annotation { "Feature Type Name" : "Feature", "Feature Type Description" : "" }
export const myFeature = defineFeature(function(context is Context, id is Id, definition is map)
    precondition{}
    {
        {
            var Q0;
            Q0=qCreatedBy(makeId("Front.planeOp"),FACE);
            var sketch = newSketch(context, id + "F0", { "sketchPlane" : qUnion([Q0])});
            skLineSegment(sketch, "E0.bottom", {"start": v(11430, -29718) * mm, "end": v(-11430, -29718) * mm});
            skLineSegment(sketch, "E0.top", {"start": v(11430, 29718) * mm, "end": v(-11430, 29718) * mm});
            skLineSegment(sketch, "E0.left", {"start": v(11430, -29718) * mm, "end": v(11430, 29718) * mm});
            skLineSegment(sketch, "E0.right", {"start": v(-11430, -29718) * mm, "end": v(-11430, 29718) * mm});
            skPoint(sketch, "E0.middle", {"position": v(0, 0) * mm});
            skPoint(sketch, "E1.endSnap0", {"position": v(0, -29718) * mm});
            skLineSegment(sketch, "E2", {"start": v(0, 0) * mm, "end": v(0, 32682.02) * mm, "construction": true});
            skLineSegment(sketch, "E3.bottom", {"start": v(-11430, -29718) * mm, "end": v(-3810, -29718) * mm});
            skLineSegment(sketch, "E3.left", {"start": v(-11430, -29718) * mm, "end": v(-11430, -22098) * mm});
            skLineSegment(sketch, "E4", {"start": v(-11430, -22098) * mm, "end": v(-3810, -22098) * mm});
            skLineSegment(sketch, "E5", {"start": v(-3810, -22098) * mm, "end": v(-3810, -29718) * mm});
            skLineSegment(sketch, "E6.bottom", {"start": v(-3810, -22098) * mm, "end": v(3810, -22098) * mm});
            skLineSegment(sketch, "E6.top", {"start": v(-3810, -29718) * mm, "end": v(3810, -29718) * mm});
            skLineSegment(sketch, "E6.right", {"start": v(3810, -22098) * mm, "end": v(3810, -29718) * mm});
            skLineSegment(sketch, "E7.bottom", {"start": v(3810, -22098) * mm, "end": v(11430, -22098) * mm});
            skLineSegment(sketch, "E7.top", {"start": v(3810, -29718) * mm, "end": v(11430, -29718) * mm});
            skLineSegment(sketch, "E7.right", {"start": v(11430, -22098) * mm, "end": v(11430, -29718) * mm});
            skLineSegment(sketch, "E8.top", {"start": v(-11430, -14478) * mm, "end": v(-3810, -14478) * mm});
            skLineSegment(sketch, "E8.left", {"start": v(-11430, -22098) * mm, "end": v(-11430, -14478) * mm});
            skLineSegment(sketch, "E8.right", {"start": v(-3810, -22098) * mm, "end": v(-3810, -14478) * mm});
            skLineSegment(sketch, "E9.top", {"start": v(-11430, -6858) * mm, "end": v(-3810, -6858) * mm});
            skLineSegment(sketch, "E9.left", {"start": v(-11430, -14478) * mm, "end": v(-11430, -6858) * mm});
            skLineSegment(sketch, "E9.right", {"start": v(-3810, -14478) * mm, "end": v(-3810, -6858) * mm});
            skLineSegment(sketch, "E10.top", {"start": v(-11430, 0) * mm, "end": v(-3810, 0) * mm});
            skLineSegment(sketch, "E10.left", {"start": v(-11430, -6858) * mm, "end": v(-11430, 0) * mm});
            skLineSegment(sketch, "E10.right", {"start": v(-3810, -6858) * mm, "end": v(-3810, 0) * mm});
            skLineSegment(sketch, "E11.top", {"start": v(-11430, 7202.75) * mm, "end": v(-3810, 7202.75) * mm});
            skLineSegment(sketch, "E11.left", {"start": v(-11430, 0) * mm, "end": v(-11430, 7202.75) * mm});
            skLineSegment(sketch, "E11.right", {"start": v(-3810, 0) * mm, "end": v(-3810, 7202.75) * mm});
            skLineSegment(sketch, "E12.top", {"start": v(-3810, -14478) * mm, "end": v(3810, -14478) * mm});
            skLineSegment(sketch, "E12.right", {"start": v(3810, -22098) * mm, "end": v(3810, -14478) * mm});
            skLineSegment(sketch, "E13.top", {"start": v(3810, -14478) * mm, "end": v(11430, -14478) * mm});
            skLineSegment(sketch, "E13.right", {"start": v(11430, -22098) * mm, "end": v(11430, -14478) * mm});
            skLineSegment(sketch, "E14.bottom", {"start": v(11430, -14478) * mm, "end": v(3810, -14478) * mm});
            skLineSegment(sketch, "E14.top", {"start": v(11430, -6858) * mm, "end": v(3810, -6858) * mm});
            skLineSegment(sketch, "E14.left", {"start": v(11430, -14478) * mm, "end": v(11430, -6858) * mm});
            skLineSegment(sketch, "E14.right", {"start": v(3810, -14478) * mm, "end": v(3810, -6858) * mm});
            skLineSegment(sketch, "E15.bottom", {"start": v(3810, -14478) * mm, "end": v(-3810, -14478) * mm});
            skLineSegment(sketch, "E15.top", {"start": v(3810, -6858) * mm, "end": v(-3810, -6858) * mm});
            skLineSegment(sketch, "E16.bottom", {"start": v(-3810, -6858) * mm, "end": v(3810, -6858) * mm});
            skLineSegment(sketch, "E16.top", {"start": v(-3810, 0) * mm, "end": v(3810, 0) * mm});
            skLineSegment(sketch, "E16.right", {"start": v(3810, -6858) * mm, "end": v(3810, 0) * mm});
            skLineSegment(sketch, "E17.bottom", {"start": v(3810, 0) * mm, "end": v(11430, 0) * mm});
            skLineSegment(sketch, "E17.top", {"start": v(3810, -6858) * mm, "end": v(11430, -6858) * mm});
            skLineSegment(sketch, "E17.left", {"start": v(3810, 0) * mm, "end": v(3810, -6858) * mm});
            skLineSegment(sketch, "E17.right", {"start": v(11430, 0) * mm, "end": v(11430, -6858) * mm});
            skLineSegment(sketch, "E18.bottom", {"start": v(11430, 0) * mm, "end": v(3810, 0) * mm});
            skLineSegment(sketch, "E18.top", {"start": v(11430, 7202.75) * mm, "end": v(3810, 7202.75) * mm});
            skLineSegment(sketch, "E18.left", {"start": v(11430, 0) * mm, "end": v(11430, 7202.75) * mm});
            skLineSegment(sketch, "E18.right", {"start": v(3810, 0) * mm, "end": v(3810, 7202.75) * mm});
            skLineSegment(sketch, "E19.bottom", {"start": v(3810, 0) * mm, "end": v(-3810, 0) * mm});
            skLineSegment(sketch, "E19.top", {"start": v(3810, 7202.75) * mm, "end": v(-3810, 7202.75) * mm});
            skSolve(sketch);
        }
        {
            var Q0;
            Q0=qCreatedBy(makeId("Front.planeOp"),FACE);
            var sketch = newSketch(context, id + "F1", { "sketchPlane" : qUnion([Q0])});
            skLineSegment(sketch, "E20.bottom", {"start": v(-4566.7, -17548.6) * mm, "end": v(-7005.1, -17548.6) * mm});
            skLineSegment(sketch, "E20.top", {"start": v(-4566.7, -16329.4) * mm, "end": v(-7005.1, -16329.4) * mm});
            skLineSegment(sketch, "E20.left", {"start": v(-4566.7, -17548.6) * mm, "end": v(-4566.7, -16329.4) * mm});
            skLineSegment(sketch, "E20.right", {"start": v(-7005.1, -17548.6) * mm, "end": v(-7005.1, -16329.4) * mm});
            skPoint(sketch, "E20.middle", {"position": v(-5785.9, -16939) * mm});
            skLineSegment(sketch, "E21.bottom", {"start": v(-7005.1, -15719.8) * mm, "end": v(-4566.7, -15719.8) * mm});
            skLineSegment(sketch, "E21.top", {"start": v(-7005.1, -14500.6) * mm, "end": v(-4566.7, -14500.6) * mm});
            skLineSegment(sketch, "E21.left", {"start": v(-7005.1, -15719.8) * mm, "end": v(-7005.1, -14500.6) * mm});
            skLineSegment(sketch, "E21.right", {"start": v(-4566.7, -15719.8) * mm, "end": v(-4566.7, -14500.6) * mm});
            skLineSegment(sketch, "E22.bottom", {"start": v(-7005.1, -13891) * mm, "end": v(-4566.7, -13891) * mm});
            skLineSegment(sketch, "E22.top", {"start": v(-7005.1, -12671.8) * mm, "end": v(-4566.7, -12671.8) * mm});
            skLineSegment(sketch, "E22.left", {"start": v(-7005.1, -13891) * mm, "end": v(-7005.1, -12671.8) * mm});
            skLineSegment(sketch, "E22.right", {"start": v(-4566.7, -13891) * mm, "end": v(-4566.7, -12671.8) * mm});
            skLineSegment(sketch, "E23.bottom", {"start": v(-7005.1, -12062.2) * mm, "end": v(-4566.7, -12062.2) * mm});
            skLineSegment(sketch, "E23.top", {"start": v(-7005.1, -10843) * mm, "end": v(-4566.7, -10843) * mm});
            skLineSegment(sketch, "E23.left", {"start": v(-7005.1, -12062.2) * mm, "end": v(-7005.1, -10843) * mm});
            skLineSegment(sketch, "E23.right", {"start": v(-4566.7, -12062.2) * mm, "end": v(-4566.7, -10843) * mm});
            skLineSegment(sketch, "E24.bottom", {"start": v(-7005.1, -10233.4) * mm, "end": v(-4566.7, -10233.4) * mm});
            skLineSegment(sketch, "E24.top", {"start": v(-7005.1, -9014.2) * mm, "end": v(-4566.7, -9014.2) * mm});
            skLineSegment(sketch, "E24.left", {"start": v(-7005.1, -10233.4) * mm, "end": v(-7005.1, -9014.2) * mm});
            skLineSegment(sketch, "E24.right", {"start": v(-4566.7, -10233.4) * mm, "end": v(-4566.7, -9014.2) * mm});
            skPoint(sketch, "E25.0", {"position": v(11430, -29718) * mm});
            skLineSegment(sketch, "E26.bottom", {"start": v(-3003.05, -3178.39) * mm, "end": v(-1631.45, -3178.39) * mm});
            skLineSegment(sketch, "E26.top", {"start": v(-2331.05, -3381.59) * mm, "end": v(-1631.45, -3381.59) * mm});
            skLineSegment(sketch, "E26.right", {"start": v(-1631.45, -3178.39) * mm, "end": v(-1631.45, -3381.59) * mm});
            skPoint(sketch, "E26.middle", {"position": v(-2317.25, -5523.3) * mm});
            skLineSegment(sketch, "E27.bottom", {"start": v(-2435.1, -9333.3) * mm, "end": v(-2199.38, -9333.3) * mm});
            skLineSegment(sketch, "E27.top", {"start": v(-2435.1, -2932.5) * mm, "end": v(-2199.38, -2932.5) * mm});
            skLineSegment(sketch, "E27.left", {"start": v(-2435.1, -9333.3) * mm, "end": v(-2435.1, -2932.5) * mm});
            skLineSegment(sketch, "E27.right", {"start": v(-2199.38, -9333.3) * mm, "end": v(-2199.38, -2932.5) * mm});
            skLineSegment(sketch, "E28.bottom", {"start": v(-1098.05, -5523.3) * mm, "end": v(-3536.45, -5523.3) * mm});
            skLineSegment(sketch, "E28.top", {"start": v(-1098.05, -4304.1) * mm, "end": v(-3536.45, -4304.1) * mm});
            skLineSegment(sketch, "E28.left", {"start": v(-1098.05, -5523.3) * mm, "end": v(-1098.05, -4304.1) * mm});
            skLineSegment(sketch, "E28.right", {"start": v(-3536.45, -5523.3) * mm, "end": v(-3536.45, -4304.1) * mm});
            skLineSegment(sketch, "E29.bottom", {"start": v(-1098.05, -7047.3) * mm, "end": v(-3536.45, -7047.3) * mm});
            skLineSegment(sketch, "E29.top", {"start": v(-1098.05, -8266.5) * mm, "end": v(-3536.45, -8266.5) * mm});
            skLineSegment(sketch, "E29.left", {"start": v(-1098.05, -7047.3) * mm, "end": v(-1098.05, -8266.5) * mm});
            skLineSegment(sketch, "E29.right", {"start": v(-3536.45, -7047.3) * mm, "end": v(-3536.45, -8266.5) * mm});
            skLineSegment(sketch, "E30.bottom", {"start": v(3290.4, -15026.65) * mm, "end": v(5728.8, -15026.65) * mm});
            skLineSegment(sketch, "E30.top", {"start": v(3290.4, -16245.85) * mm, "end": v(5728.8, -16245.85) * mm});
            skLineSegment(sketch, "E30.left", {"start": v(3290.4, -15026.65) * mm, "end": v(3290.4, -16245.85) * mm});
            skLineSegment(sketch, "E30.right", {"start": v(5728.8, -15026.65) * mm, "end": v(5728.8, -16245.85) * mm});
            skLineSegment(sketch, "E31.bottom", {"start": v(3290.4, -16855.45) * mm, "end": v(5728.8, -16855.45) * mm});
            skLineSegment(sketch, "E31.top", {"start": v(3290.4, -18074.65) * mm, "end": v(5728.8, -18074.65) * mm});
            skLineSegment(sketch, "E31.left", {"start": v(3290.4, -16855.45) * mm, "end": v(3290.4, -18074.65) * mm});
            skLineSegment(sketch, "E31.right", {"start": v(5728.8, -16855.45) * mm, "end": v(5728.8, -18074.65) * mm});
            skLineSegment(sketch, "E32.bottom", {"start": v(3290.4, -14417.05) * mm, "end": v(5728.8, -14417.05) * mm});
            skLineSegment(sketch, "E32.top", {"start": v(3290.4, -13197.85) * mm, "end": v(5728.8, -13197.85) * mm});
            skLineSegment(sketch, "E32.left", {"start": v(3290.4, -14417.05) * mm, "end": v(3290.4, -13197.85) * mm});
            skLineSegment(sketch, "E32.right", {"start": v(5728.8, -14417.05) * mm, "end": v(5728.8, -13197.85) * mm});
            skLineSegment(sketch, "E33.bottom", {"start": v(5728.8, -12588.25) * mm, "end": v(3290.4, -12588.25) * mm});
            skLineSegment(sketch, "E33.top", {"start": v(5728.8, -11369.05) * mm, "end": v(3290.4, -11369.05) * mm});
            skLineSegment(sketch, "E33.left", {"start": v(5728.8, -12588.25) * mm, "end": v(5728.8, -11369.05) * mm});
            skLineSegment(sketch, "E33.right", {"start": v(3290.4, -12588.25) * mm, "end": v(3290.4, -11369.05) * mm});
            skPoint(sketch, "E34.0", {"position": v(-11430, -29718) * mm});
            skLineSegment(sketch, "E35.bottom", {"start": v(-6979.92, -27259.75) * mm, "end": v(-4541.52, -27259.75) * mm});
            skLineSegment(sketch, "E35.top", {"start": v(-6979.92, -25453.56) * mm, "end": v(-4541.52, -25453.56) * mm});
            skLineSegment(sketch, "E35.left", {"start": v(-6979.92, -27259.75) * mm, "end": v(-6979.92, -25453.56) * mm});
            skLineSegment(sketch, "E35.right", {"start": v(-4541.52, -27259.75) * mm, "end": v(-4541.52, -25453.56) * mm});
            skLineSegment(sketch, "E36.bottom", {"start": v(3290.4, -10759.45) * mm, "end": v(5728.8, -10759.45) * mm});
            skLineSegment(sketch, "E36.top", {"start": v(3290.4, -9540.25) * mm, "end": v(5728.8, -9540.25) * mm});
            skLineSegment(sketch, "E36.left", {"start": v(3290.4, -10759.45) * mm, "end": v(3290.4, -9540.25) * mm});
            skLineSegment(sketch, "E36.right", {"start": v(5728.8, -10759.45) * mm, "end": v(5728.8, -9540.25) * mm});
            skLineSegment(sketch, "E37.bottom", {"start": v(11436.49, -48.33) * mm, "end": v(8998.09, -48.33) * mm});
            skLineSegment(sketch, "E37.top", {"start": v(11436.49, -9192.33) * mm, "end": v(8998.09, -9192.33) * mm});
            skLineSegment(sketch, "E37.left", {"start": v(11436.49, -48.33) * mm, "end": v(11436.49, -9192.33) * mm});
            skLineSegment(sketch, "E37.right", {"start": v(8998.09, -48.33) * mm, "end": v(8998.09, -9192.33) * mm});
            skLineSegment(sketch, "E38.bottom", {"start": v(-2991.86, -8977.7) * mm, "end": v(-1620.26, -8977.7) * mm});
            skLineSegment(sketch, "E38.top", {"start": v(-2319.86, -9180.9) * mm, "end": v(-1620.26, -9180.9) * mm});
            skLineSegment(sketch, "E38.right", {"start": v(-1620.26, -8977.7) * mm, "end": v(-1620.26, -9180.9) * mm});
            skLineSegment(sketch, "E39.bottom", {"start": v(7271.07, -20654.4) * mm, "end": v(7271.07, -22026) * mm});
            skLineSegment(sketch, "E39.top", {"start": v(7067.87, -20654.4) * mm, "end": v(7067.87, -22026) * mm});
            skLineSegment(sketch, "E39.left", {"start": v(7943.07, -20654.4) * mm, "end": v(7067.87, -20654.4) * mm});
            skLineSegment(sketch, "E39.right", {"start": v(7271.07, -22026) * mm, "end": v(7067.87, -22026) * mm});
            skPoint(sketch, "E39.middle", {"position": v(4926.16, -21340.2) * mm});
            skLineSegment(sketch, "E40.bottom", {"start": v(1573.36, -21222.33) * mm, "end": v(1573.36, -21458.06) * mm});
            skLineSegment(sketch, "E40.top", {"start": v(7974.16, -21222.33) * mm, "end": v(7974.16, -21458.06) * mm});
            skLineSegment(sketch, "E40.left", {"start": v(1573.36, -21222.33) * mm, "end": v(7974.16, -21222.33) * mm});
            skLineSegment(sketch, "E40.right", {"start": v(1573.36, -21458.06) * mm, "end": v(7974.16, -21458.06) * mm});
            skLineSegment(sketch, "E41.bottom", {"start": v(1471.76, -20665.59) * mm, "end": v(1471.76, -22037.19) * mm});
            skLineSegment(sketch, "E41.top", {"start": v(1268.56, -20665.59) * mm, "end": v(1268.56, -22037.19) * mm});
            skLineSegment(sketch, "E41.left", {"start": v(2143.76, -20665.59) * mm, "end": v(1268.56, -20665.59) * mm});
            skLineSegment(sketch, "E41.right", {"start": v(1471.76, -22037.19) * mm, "end": v(1268.56, -22037.19) * mm});
            skPoint(sketch, "E42.firstSnap0", {"position": v(-10210.8, 0) * mm});
            skLineSegment(sketch, "E43.bottom", {"start": v(-9601.2, -487.68) * mm, "end": v(-8382, -487.68) * mm});
            skLineSegment(sketch, "E43.top", {"start": v(-9601.2, -1706.88) * mm, "end": v(-8382, -1706.88) * mm});
            skLineSegment(sketch, "E43.left", {"start": v(-9601.2, -487.68) * mm, "end": v(-9601.2, -1706.88) * mm});
            skLineSegment(sketch, "E43.right", {"start": v(-8382, -487.68) * mm, "end": v(-8382, -1706.88) * mm});
            skLineSegment(sketch, "E44.bottom", {"start": v(-7620, -286.18) * mm, "end": v(-6781.8, -286.18) * mm});
            skLineSegment(sketch, "E44.top", {"start": v(-7620, 628.22) * mm, "end": v(-6781.8, 628.22) * mm});
            skLineSegment(sketch, "E44.left", {"start": v(-7620, -286.18) * mm, "end": v(-7620, 628.22) * mm});
            skLineSegment(sketch, "E44.right", {"start": v(-6781.8, -286.18) * mm, "end": v(-6781.8, 628.22) * mm});
            skLineSegment(sketch, "E45.bottom", {"start": v(-4907.28, 0) * mm, "end": v(-4907.28, 609.6) * mm});
            skLineSegment(sketch, "E45.top", {"start": v(-6126.48, 0) * mm, "end": v(-6126.48, 609.6) * mm});
            skLineSegment(sketch, "E45.left", {"start": v(-4907.28, 0) * mm, "end": v(-6126.48, 0) * mm});
            skLineSegment(sketch, "E45.right", {"start": v(-4907.28, 609.6) * mm, "end": v(-6126.48, 609.6) * mm});
            skLineSegment(sketch, "E46.bottom", {"start": v(11059.57, -29081.73) * mm, "end": v(8113.97, -29081.73) * mm});
            skLineSegment(sketch, "E46.top", {"start": v(11059.57, -22741.37) * mm, "end": v(8113.97, -22741.37) * mm});
            skLineSegment(sketch, "E46.left", {"start": v(11059.57, -29081.73) * mm, "end": v(11059.57, -22741.37) * mm});
            skLineSegment(sketch, "E46.right", {"start": v(8113.97, -29081.73) * mm, "end": v(8113.97, -22741.37) * mm});
            skLineSegment(sketch, "E47.bottom", {"start": v(-6124.47, -5694.77) * mm, "end": v(-8562.87, -5694.77) * mm});
            skLineSegment(sketch, "E47.top", {"start": v(-6124.47, -4475.57) * mm, "end": v(-8562.87, -4475.57) * mm});
            skLineSegment(sketch, "E47.left", {"start": v(-6124.47, -5694.77) * mm, "end": v(-6124.47, -4475.57) * mm});
            skLineSegment(sketch, "E47.right", {"start": v(-8562.87, -5694.77) * mm, "end": v(-8562.87, -4475.57) * mm});
            skLineSegment(sketch, "E48.top", {"start": v(11436.49, -12871.82) * mm, "end": v(8388.49, -12871.82) * mm});
            skLineSegment(sketch, "E48.left", {"start": v(11436.49, -15919.82) * mm, "end": v(11436.49, -12871.82) * mm});
            skLineSegment(sketch, "E49", {"start": v(8388.49, -12871.82) * mm, "end": v(8388.49, -15919.82) * mm});
            skLineSegment(sketch, "E50", {"start": v(8388.49, -15919.82) * mm, "end": v(11436.49, -15919.82) * mm});
            skLineSegment(sketch, "E51.bottom", {"start": v(-10515.6, 2200.76) * mm, "end": v(-9601.2, 2200.76) * mm});
            skLineSegment(sketch, "E51.top", {"start": v(-10515.6, 3419.96) * mm, "end": v(-9601.2, 3419.96) * mm});
            skLineSegment(sketch, "E51.left", {"start": v(-10515.6, 2200.76) * mm, "end": v(-10515.6, 3419.96) * mm});
            skLineSegment(sketch, "E51.right", {"start": v(-9601.2, 2200.76) * mm, "end": v(-9601.2, 3419.96) * mm});
            skLineSegment(sketch, "E52.bottom", {"start": v(-6944.14, -23095.97) * mm, "end": v(-4505.74, -23095.97) * mm});
            skLineSegment(sketch, "E52.top", {"start": v(-6944.14, -21876.77) * mm, "end": v(-4505.74, -21876.77) * mm});
            skLineSegment(sketch, "E52.left", {"start": v(-6944.14, -23095.97) * mm, "end": v(-6944.14, -21876.77) * mm});
            skLineSegment(sketch, "E52.right", {"start": v(-4505.74, -23095.97) * mm, "end": v(-4505.74, -21876.77) * mm});
            skLineSegment(sketch, "E53.bottom", {"start": v(-6944.14, -21267.17) * mm, "end": v(-4505.74, -21267.17) * mm});
            skLineSegment(sketch, "E53.top", {"start": v(-6944.14, -20047.97) * mm, "end": v(-4505.74, -20047.97) * mm});
            skLineSegment(sketch, "E53.left", {"start": v(-6944.14, -21267.17) * mm, "end": v(-6944.14, -20047.97) * mm});
            skLineSegment(sketch, "E53.right", {"start": v(-4505.74, -21267.17) * mm, "end": v(-4505.74, -20047.97) * mm});
            skLineSegment(sketch, "E54.bottom", {"start": v(-6944.14, -19438.37) * mm, "end": v(-4505.74, -19438.37) * mm});
            skLineSegment(sketch, "E54.top", {"start": v(-6944.14, -18219.17) * mm, "end": v(-4505.74, -18219.17) * mm});
            skLineSegment(sketch, "E54.left", {"start": v(-6944.14, -19438.37) * mm, "end": v(-6944.14, -18219.17) * mm});
            skLineSegment(sketch, "E54.right", {"start": v(-4505.74, -19438.37) * mm, "end": v(-4505.74, -18219.17) * mm});
            skLineSegment(sketch, "E55.bottom", {"start": v(3290.4, -7809.3) * mm, "end": v(5728.8, -7809.3) * mm});
            skLineSegment(sketch, "E55.top", {"start": v(3290.4, -9028.5) * mm, "end": v(5728.8, -9028.5) * mm});
            skLineSegment(sketch, "E55.left", {"start": v(3290.4, -7809.3) * mm, "end": v(3290.4, -9028.5) * mm});
            skLineSegment(sketch, "E55.right", {"start": v(5728.8, -7809.3) * mm, "end": v(5728.8, -9028.5) * mm});
            skLineSegment(sketch, "E56.bottom", {"start": v(3290.4, -7199.7) * mm, "end": v(5728.8, -7199.7) * mm});
            skLineSegment(sketch, "E56.top", {"start": v(3290.4, -5980.5) * mm, "end": v(5728.8, -5980.5) * mm});
            skLineSegment(sketch, "E56.left", {"start": v(3290.4, -7199.7) * mm, "end": v(3290.4, -5980.5) * mm});
            skLineSegment(sketch, "E56.right", {"start": v(5728.8, -7199.7) * mm, "end": v(5728.8, -5980.5) * mm});
            skLineSegment(sketch, "E57.bottom", {"start": v(5728.8, -5370.9) * mm, "end": v(3290.4, -5370.9) * mm});
            skLineSegment(sketch, "E57.top", {"start": v(5728.8, -4151.7) * mm, "end": v(3290.4, -4151.7) * mm});
            skLineSegment(sketch, "E57.left", {"start": v(5728.8, -5370.9) * mm, "end": v(5728.8, -4151.7) * mm});
            skLineSegment(sketch, "E57.right", {"start": v(3290.4, -5370.9) * mm, "end": v(3290.4, -4151.7) * mm});
            skSolve(sketch);
        }
        {
            var Q0;
            Q0 = qSketchRegion(id + "F1", true);
            extrude(context, id + "F2", {"entities" : qUnion([Q0]), "depth" : 30.48 * mm, "offsetDistance" : 30.48 * mm});
        }
        {
            var Q0;
            Q0 = qSketchRegion(id + "F0", true);
            var Q1;
            Q1=makeQuery(id+"F0.imprint","IMPRINT",FACE,{"disambiguationData":[TD([[makeQuery(id+"F0.imprint","IMPRINT",EDGE,{"derivedFrom":sQuery(id+"F0.wireOp",EDGE,"E19.bottom")}),-1.0]])]});
            var Q2;
            Q2=makeQuery(id+"F0.imprint","IMPRINT",FACE,{"disambiguationData":[TD([[makeQuery(id+"F0.imprint","IMPRINT",EDGE,{"derivedFrom":sQuery(id+"F0.wireOp",EDGE,"E16.bottom")}),1.0]])]});
            var Q3;
            Q3=makeQuery(id+"F0.imprint","IMPRINT",FACE,{"disambiguationData":[TD([[makeQuery(id+"F0.imprint","IMPRINT",EDGE,{"derivedFrom":sQuery(id+"F0.wireOp",EDGE,"E15.bottom")}),-1.0]])]});
            var Q4;
            Q4=makeQuery(id+"F0.imprint","IMPRINT",FACE,{"disambiguationData":[TD([[makeQuery(id+"F0.imprint","IMPRINT",EDGE,{"derivedFrom":sQuery(id+"F0.wireOp",EDGE,"E6.bottom")}),1.0]])]});
            extrude(context, id + "F3", {"entities" : qUnion([Q0, Q1, Q2, Q3, Q4]), "depth" : 30.48 * mm, "offsetDistance" : 30.48 * mm});
        }
        {
            var Q0;
            Q0=sQuery(id+"F1.wireOp",EDGE,"E52.bottom");
            var Q1;
            Q1=sQuery(id+"F1.wireOp",EDGE,"E53.top");
            var Q2;
            Q2=sQuery(id+"F1.wireOp",EDGE,"E54.top");
            var Q3;
            Q3=sQuery(id+"F1.wireOp",EDGE,"E53.left");
            var Q4;
            Q4=sQuery(id+"F1.wireOp",EDGE,"E52.top");
            var Q5;
            Q5=sQuery(id+"F1.wireOp",EDGE,"E52.right");
            var Q6;
            Q6=sQuery(id+"F1.wireOp",EDGE,"E54.left");
            var Q7;
            Q7=sQuery(id+"F1.wireOp",EDGE,"E52.left");
            var Q8;
            Q8=sQuery(id+"F1.wireOp",EDGE,"E54.right");
            var Q9;
            Q9=sQuery(id+"F1.wireOp",EDGE,"E53.bottom");
            var Q10;
            Q10=sQuery(id+"F1.wireOp",EDGE,"E53.right");
            var Q11;
            Q11=sQuery(id+"F1.wireOp",EDGE,"E54.bottom");
            extrude(context, id + "F4", {"bodyType" : ToolBodyType.SURFACE, "surfaceEntities" : qUnion([Q0, Q1, Q2, Q3, Q4, Q5, Q6, Q7, Q8, Q9, Q10, Q11]), "depth" : 121.92 * mm, "offsetDistance" : 30.48 * mm});
        }
        {
            var Q0;
            Q0=makeQuery(id+"F3.opExtrude","CAP_FACE",FACE,{"disambiguationData":[OSD([sQuery(id+"F0.wireOp",EDGE,"E0.top"),sQuery(id+"F0.wireOp",EDGE,"E0.left"),sQuery(id+"F0.wireOp",EDGE,"E0.right"),sQuery(id+"F0.wireOp",EDGE,"E3.bottom"),sQuery(id+"F0.wireOp",EDGE,"E3.left"),sQuery(id+"F0.wireOp",EDGE,"E6.top"),sQuery(id+"F0.wireOp",EDGE,"E7.top"),sQuery(id+"F0.wireOp",EDGE,"E7.right"),sQuery(id+"F0.wireOp",EDGE,"E8.left"),sQuery(id+"F0.wireOp",EDGE,"E9.left"),sQuery(id+"F0.wireOp",EDGE,"E10.left"),sQuery(id+"F0.wireOp",EDGE,"E11.left"),sQuery(id+"F0.wireOp",EDGE,"E13.right"),sQuery(id+"F0.wireOp",EDGE,"E14.left"),sQuery(id+"F0.wireOp",EDGE,"E17.right"),sQuery(id+"F0.wireOp",EDGE,"E18.left")])],"isStart":false});
            var sketch = newSketch(context, id + "F5", { "sketchPlane" : qUnion([Q0])});
            skText(sketch, "E58", { "text": "Backsheet Build\n10 min", "fontName": "Tinos-Bold.ttf"});
            const initialGuessF5  = {"E58": [-6.73608, -26.288, 1, 0, 0.18893]};
            skSetInitialGuess(sketch, initialGuessF5);
            skSolve(sketch);
        }
        {
            var Q0;
            Q0 = qSketchRegion(id + "F5", true);
            extrude(context, id + "F6", {"entities" : qUnion([Q0]), "operationType" : NewBodyOperationType.REMOVE, "oppositeDirection" : true, "depth" : 609.6 * mm, "offsetDistance" : 30.48 * mm});
        }
        {
            var Q0;
            Q0=qCreatedBy(makeId("Front.planeOp"),FACE);
            var sketch = newSketch(context, id + "F7", { "sketchPlane" : qUnion([Q0])});
            skText(sketch, "E59", { "text": "Lay Foam and Sealing\n15 min", "fontName": "OpenSans-Regular.ttf"});
            const initialGuessF7  = {"E59": [-6.6623, -22.48313, 1, 0, 0.13008]};
            skSetInitialGuess(sketch, initialGuessF7);
            skSolve(sketch);
        }
        {
            var Q0;
            Q0=qCreatedBy(makeId("Front.planeOp"),FACE);
            var sketch = newSketch(context, id + "F8", { "sketchPlane" : qUnion([Q0])});
            skText(sketch, "E60", { "text": "Cure", "fontName": "OpenSans-Regular.ttf"});
            skText(sketch, "E61", { "text": "Cure", "fontName": "OpenSans-Regular.ttf"});
            const initialGuessF8  = {"E60": [-6.61416, -20.93653, 1, 0, 0.59138], "E61": [-6.69727, -19.08162, 1, 0, 0.59138]};
            skSetInitialGuess(sketch, initialGuessF8);
            skSolve(sketch);
        }
        {
            var Q0;
            Q0 = qSketchRegion(id + "F7", true);
            extrude(context, id + "F9", {"entities" : qUnion([Q0]), "operationType" : NewBodyOperationType.REMOVE, "depth" : 609.6 * mm, "offsetDistance" : 30.48 * mm});
        }
        {
            var Q0;
            Q0 = qSketchRegion(id + "F8", true);
            extrude(context, id + "F10", {"entities" : qUnion([Q0]), "operationType" : NewBodyOperationType.REMOVE, "depth" : 609.6 * mm, "offsetDistance" : 30.48 * mm});
        }
    });